# Revit family: Воздухоудалитель с функцией впуска и выпуска воздуха 2630 02
name_source: partatom
category: Rohrzubehör
revit_build: Autodesk Revit 2018 (Build: 20190510_1515(x64)
units: mm (PartAtom-declared; Revit-internal decimal feet)

## family parameters
Arbeitsebenenbasiert = Nein
Beim Laden mit Abzugskörper schneiden = Nein
Bemaßung runder Anschluss = Durchmesser verwenden
Gemeinsam genutzt = Nein
Immer vertikal = Ja
OmniClass-Nummer = 23.65.55.14
OmniClass-Titel = Valves for Liquid Services
Teiletyp = Normal

## types (1)
- Воздухоудалитель с функцией впуска и выпуска воздуха 2630 02
    D01 = 16.2 mm  [stored 0.0531496 ft]
    D02 = 19.5 mm  [stored 0.0639764 ft]
    D03 = 5.1 mm  [stored 0.0167323 ft]
    D04 = 3.4 mm  [stored 0.0111549 ft]
    D05 = 0.8 mm  [stored 0.00262467 ft]
    H00 = 59 mm
    H01 = 12 mm  [stored 0.0393701 ft]
    H02 = 9.5 mm  [stored 0.031168 ft]
    H03 = 63 mm  [stored 0.206693 ft]
    H04 = 57.9 mm  [stored 0.189961 ft]
    H05 = 58 mm  [stored 0.190289 ft]
    Hersteller = Herz-Armaturen GmbH
    L00 = 33.5 mm
    L01 = 9.5 mm  [stored 0.031168 ft]
    L02 = 4.8 mm  [stored 0.015748 ft]
    L03 = 13.5 mm  [stored 0.0442913 ft]
    L04 = 24 mm  [stored 0.0787402 ft]
    R01 = 2 mm  [stored 0.00656168 ft]
    S01 = 24.5 mm  [stored 0.0803806 ft]
    S02 = 11 mm  [stored 0.0360892 ft]
    SCRNCODE = 05;14;01
    SCRNSEQ = AWI;AWI_TYP="1013";1
    URL = www.herz-armaturen.ru
    Колпачок = полипропилен, цвет черный
    Корпус = штампованная латунь в соответствии с EN 12165, CW617N
    Крышка корпуса = штампованная латунь в соответствии с EN 12165, CW617N
    Макс. давление на корпусе = 1200000.0 Pa
    Макс. рабочая температура = 110 °C
    Макс. рабочее давление = 800000.0 Pa
    Мин. рабочая температура = 0 °C
    Наружная резьба подключения = в соответствии с ISO 228
    Область применения = Воздухоотводчик используется для удаления воздуха в системах отопления и холодоснабжения. Клапаны должны быть размещены рядом с котлом или же в самых высоких точках системы, чтобы обеспечить удаление воздуха из системы.
    Поплавок = полипропилен
    Среда = Качество  теплоносителя в соответствии с ÖNORM H5195 и/или предписаниями VDI-Standard 2035.
Разрешается использование смеси этилен или пропиленгликоля в соотношении 25-50% с водой. Прокладки EPDM могут быть подвержены воздействию минеральных смазочных масел, что может служить причиной выхода из строя данных уплотнений. Пожалуйста, обратитесь к документации производителя, при использовании этиленгликоля и пропиленгликоля в целях защиты от замерзания.
    Уплотнение = NBR

note: [stored X ft] marks values corroborated as IEEE doubles in the binary element streams (Revit-internal decimal feet)
